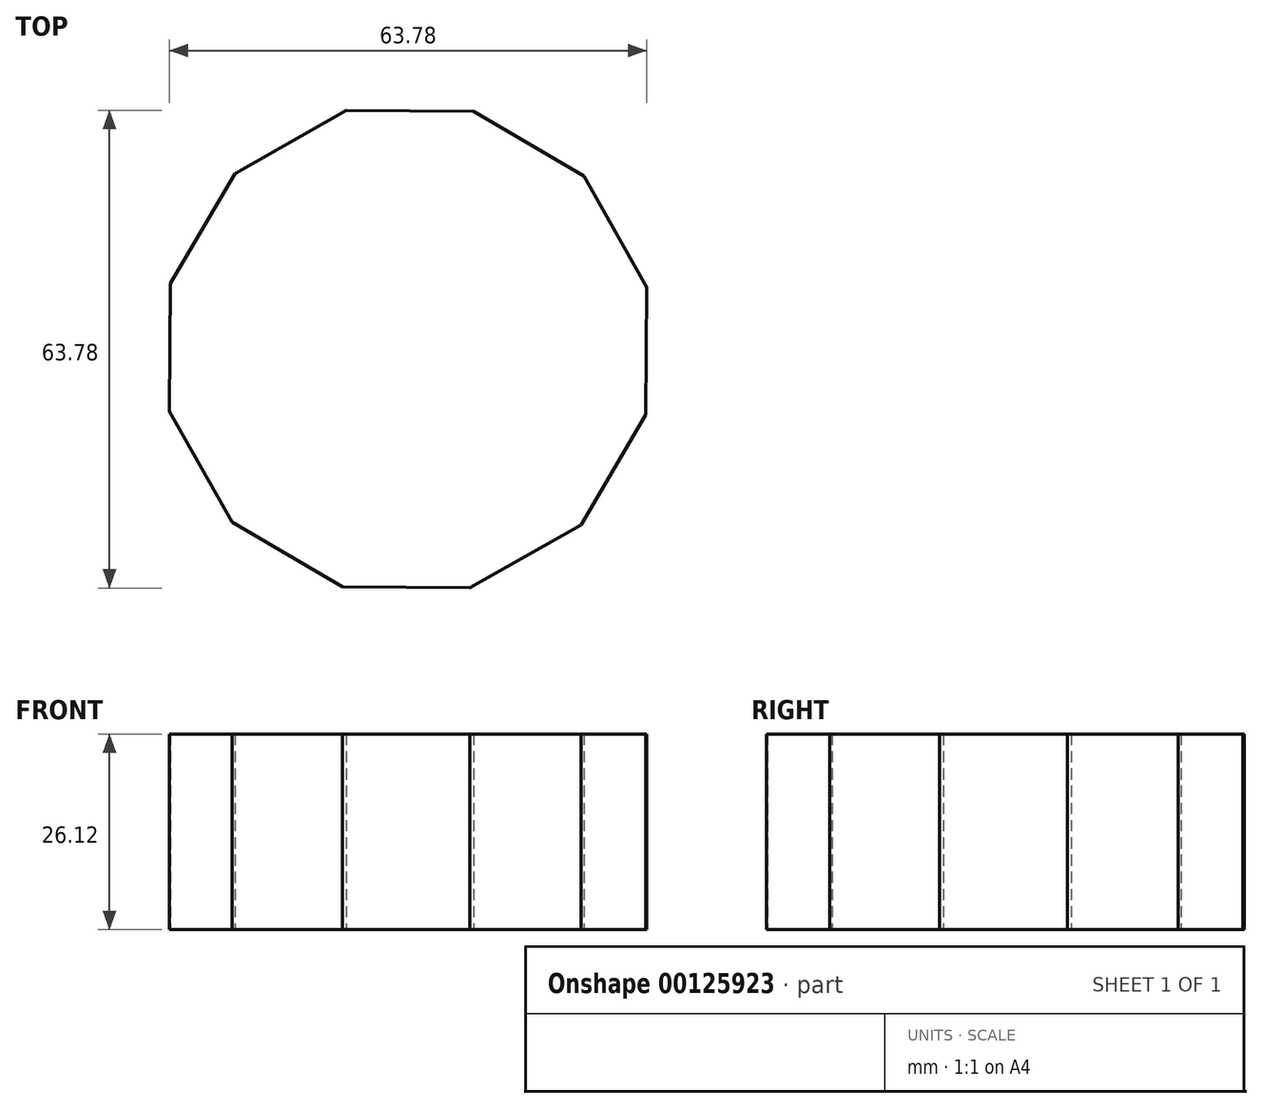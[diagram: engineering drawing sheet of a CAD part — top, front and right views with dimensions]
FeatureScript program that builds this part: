
annotation { "Feature Type Name" : "Feature", "Feature Type Description" : "" }
export const myFeature = defineFeature(function(context is Context, id is Id, definition is map)
    precondition{}
    {
        {
            var Q0;
            Q0=qCreatedBy(makeId("Top.planeOp"),FACE);
            var sketch = newSketch(context, id + "F0", { "sketchPlane" : qUnion([Q0])});
            skCircle(sketch, "E0.cCircle", {"center": v(0, 0) * mm, "radius": 31.82 * mm, "construction": true});
            skLineSegment(sketch, "E0.0", {"start": v(8.77, 31.75) * mm, "end": v(23.47, 23.11) * mm});
            skLineSegment(sketch, "E0.1", {"start": v(23.47, 23.11) * mm, "end": v(31.89, 8.28) * mm});
            skLineSegment(sketch, "E0.2", {"start": v(31.89, 8.28) * mm, "end": v(31.75, -8.77) * mm});
            skLineSegment(sketch, "E0.3", {"start": v(31.75, -8.77) * mm, "end": v(23.11, -23.47) * mm});
            skLineSegment(sketch, "E0.4", {"start": v(23.11, -23.47) * mm, "end": v(8.28, -31.89) * mm});
            skLineSegment(sketch, "E0.5", {"start": v(8.28, -31.89) * mm, "end": v(-8.77, -31.75) * mm});
            skLineSegment(sketch, "E0.6", {"start": v(-8.77, -31.75) * mm, "end": v(-23.47, -23.11) * mm});
            skLineSegment(sketch, "E0.7", {"start": v(-23.47, -23.11) * mm, "end": v(-31.89, -8.28) * mm});
            skLineSegment(sketch, "E0.8", {"start": v(-31.89, -8.28) * mm, "end": v(-31.75, 8.77) * mm});
            skLineSegment(sketch, "E0.9", {"start": v(-31.75, 8.77) * mm, "end": v(-23.11, 23.47) * mm});
            skLineSegment(sketch, "E0.10", {"start": v(-23.11, 23.47) * mm, "end": v(-8.28, 31.89) * mm});
            skLineSegment(sketch, "E0.11", {"start": v(-8.28, 31.89) * mm, "end": v(8.77, 31.75) * mm});
            skPoint(sketch, "E0.0.midPoint", {"position": v(16.12, 27.43) * mm});
            skSolve(sketch);
        }
        {
            var Q0;
            Q0 = qSketchRegion(id + "F0", true);
            extrude(context, id + "F1", {"entities" : qUnion([Q0]), "depth" : 26.12 * mm});
        }
    });
